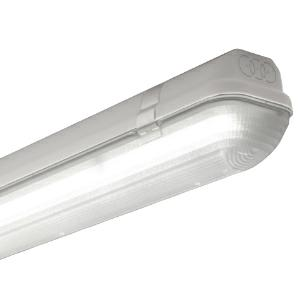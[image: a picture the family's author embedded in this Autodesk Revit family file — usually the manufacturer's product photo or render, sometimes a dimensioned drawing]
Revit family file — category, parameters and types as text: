
# Revit family: 3f_filippi_-_3f_linda_3f_filippi_-_58591_-_3f_linda_led_1x24w-830_ep_l1270
name_source: partatom
category: Lighting Fixtures
units: mm (PartAtom-declared; Revit-internal decimal feet)

## family parameters
Cut with Voids When Loaded = No
Host = Face
Light Source = No
Part Type = Normal
Room Calculation Point = No
Round Connector Dimension = Use Diameter
Shared = No

## types (1)
- 3F Filippi - 3F Linda (1 x LED, 3862 lm, 29 W, 3000 K)
    Apparent Load = 29 VA
    Approval mark = ENEC
    CIE Flux Codes = 44 77 94 97 100
    Color Rendering = 80
    Color Temperature = 3000 K
    Control Gear = Electronic ballast
    Default Elevation = 1800 mm
    Description = ILLUMINOTECHNICAL
Luminous efficiency 100% (DLOR 97%, ULOR 3%).
Initial luminous flux of the luminaire 3862 lm.
Emergency luminaire luminous flux BLF 14.3%.
Controlled symmetric distribution.
Installation Interdistance Transv.D = 1.77 x hu - Long.D = 1.17 x hu.
Tabular UGR (CIE 117 - 4H-8H; S=0.25H; 70/50/20): RUG 21.8 - 22.7.
Beam angle: 109° - 64°.
Luminous efficacy 133 lm/W.
Lifetime (L93/B10): 30000 h. (tq+25°C)
Lifetime (L90/B10): 50000 h. (tq+25°C)
Lifetime (L85/B10): 80000 h. (tq+25°C)
Lifetime (L80/B10): 100000 h. (tq+25°C)
Sudden decreased luminous flux after 50000 hours: 0% (C0).
Photobiological safety in compliance with IEC/TR 62778: RG0 risk exempt, (IEC 62471).
In compliance with IEC/EN 62722-2-1 - IEC/EN 62717 standards.

SOURCE
Linear LED module 24W/830.
Energy efficiency class (UE 2019/2020 - UE 2019/2015): D.
CIE 13.3 Colour rendering index: CRI >80 (R9 <50%).
IES TM-30 Fidelity Index: Rf = 84 Rg = 95.
CCT nominal colour temperature 3000 K.
Colour initial tolerance (MacAdam): SDCM 3.

MECHANICAL
Self-extinguishing V2 polycarbonate housing, injection moulded, RAL 7035 grey.
Ecologic anti-aging injected sealing gasket.
Diffuser in self-extinguishing V2 polycarbonate, photo-engraved interior, UV stabilised, injection moulded with smooth outer surface, tamper-proof opening.
Gear-holder reflector in hot-dip galvanised steel, painted with white polyester base.
Snug fit safety snap-lock clips for diffuser mounting in stainless steel, screwdriver opening.
Fixing brackets in stainless steel.
Possibility for technicians to access the interior of the luminaire.
Luminaire with limited surface temperature. - D - (EN 60598-2-24)
Dimensions: 1270x100 mm, height 100 mm. Weight 2.49 kg.
IP66 protection degree.
Mechanical strength to impacts IK10 (20 joule).
Glow-wire test resistance 850°C.

ELECTRICAL
Halogen Free electronic wiring 230V-50/60Hz, power factor 0.90, THD <25%, constant output current, SELV, class I, 1 driver.
Power of the luminaire 29 W.
CE - IEC 60598-1 - EN 60598-1.
EP maintained emergency wiring on board, 1h duration, 24h recharge; compliant with EN 60598-2-22, excluding high risk areas.
SAFE FLICKER: PstLM=<1 and SVM=<0.4 (IEC TR 61547-1 and IEC TR 63158), to ensure a more comfortable and safe light.
Ambient temperature from +5°C to +25°C.
Temperature class T6 max 85°C.
Relative humidity UR: <85%.

INSTALLATION
Ceiling / Suspended / Wall.
All accessories dedicated to this product are available on the Catalog and on our website www.3F-Filippi.com.

APPLICATIONS
Suitable product for food production plants (HACCP), IFS (Food Version 6), BRC (GSFS Food Version 7).
Dry, dusty indoor environments, subject to occasional water splashes.
Virtually shatterproof polycarbonate compatibly with the fumes / atmospheres that compromise the elasticity of plastic materials.
Not suitable for installation on surfaces subject to important vibrations, exposed to weather conditions, on ropes or poles.
Suitable for illumination of public car parks and parking grounds referred to DIN 67528:2018-04.

WARNING
Fixture not suitable for cold stores with an ambient temperature <5°C and/or relative humidity >85%.
Luminaire designed for disposal/recycling at end-of-life.
Replaceable (LED only) light source by a professional. Replaceable control gear by a professional.
    Height = 100 mm  [stored 0.328084 ft]
    Lamp = 1 x LED
    Lamp Light Flux = 3862 lm
    Lamp Power = 29 W
    Lamp count = 1
    Length = 1270 mm
    Lifetime = 50000 h
    Luminous efficacy = 133 lm/W
    Manufacturer = 3F Filippi
    ModVariant = No
    Model = 3F Filippi - 58591 - 3F Linda LED 1x24W-830 EP L1270
    Mounting Place = Ceiling
    Mounting Type = Pendant
    Number of Poles = 1
    OnlyDefault = Yes
    Power Factor = 1
    Product Name = 3F Filippi - 3F Linda
    Product group = pendant luminaire
    ProductGroupID = 9
    Protection Class = Protection class I
    Protection Degree = IP 66
    RLX_Detail_Level = 1
    RLX_Emergency_Light_Flux = 0 lm
    RLX_Emergency_Type = 0
    RLX_Emergency_Type_DB = No
    RlxData = <blob elided: 70389 chars, md5=411da6be>
    Socket = socket
    Standby Power = 0 W
    System Light Flux = 3862 lm
    System Power = 29 W
    Type Comments = Product without accessories
    Type Image = 3ffilippi_3f_linda_led.jpg
    URL = http://relux.com
    VarID = ---
    Voltage = 0 V
    Weight = 0.00 kg
    Width = 100 mm  [stored 0.328084 ft]

note: [stored X ft] marks values corroborated as IEEE doubles in the binary element streams (Revit-internal decimal feet)

## geometry (parser evidence)
native form markers: Blend x4, Sweep x10
no freeform markers — native parametric forms only
